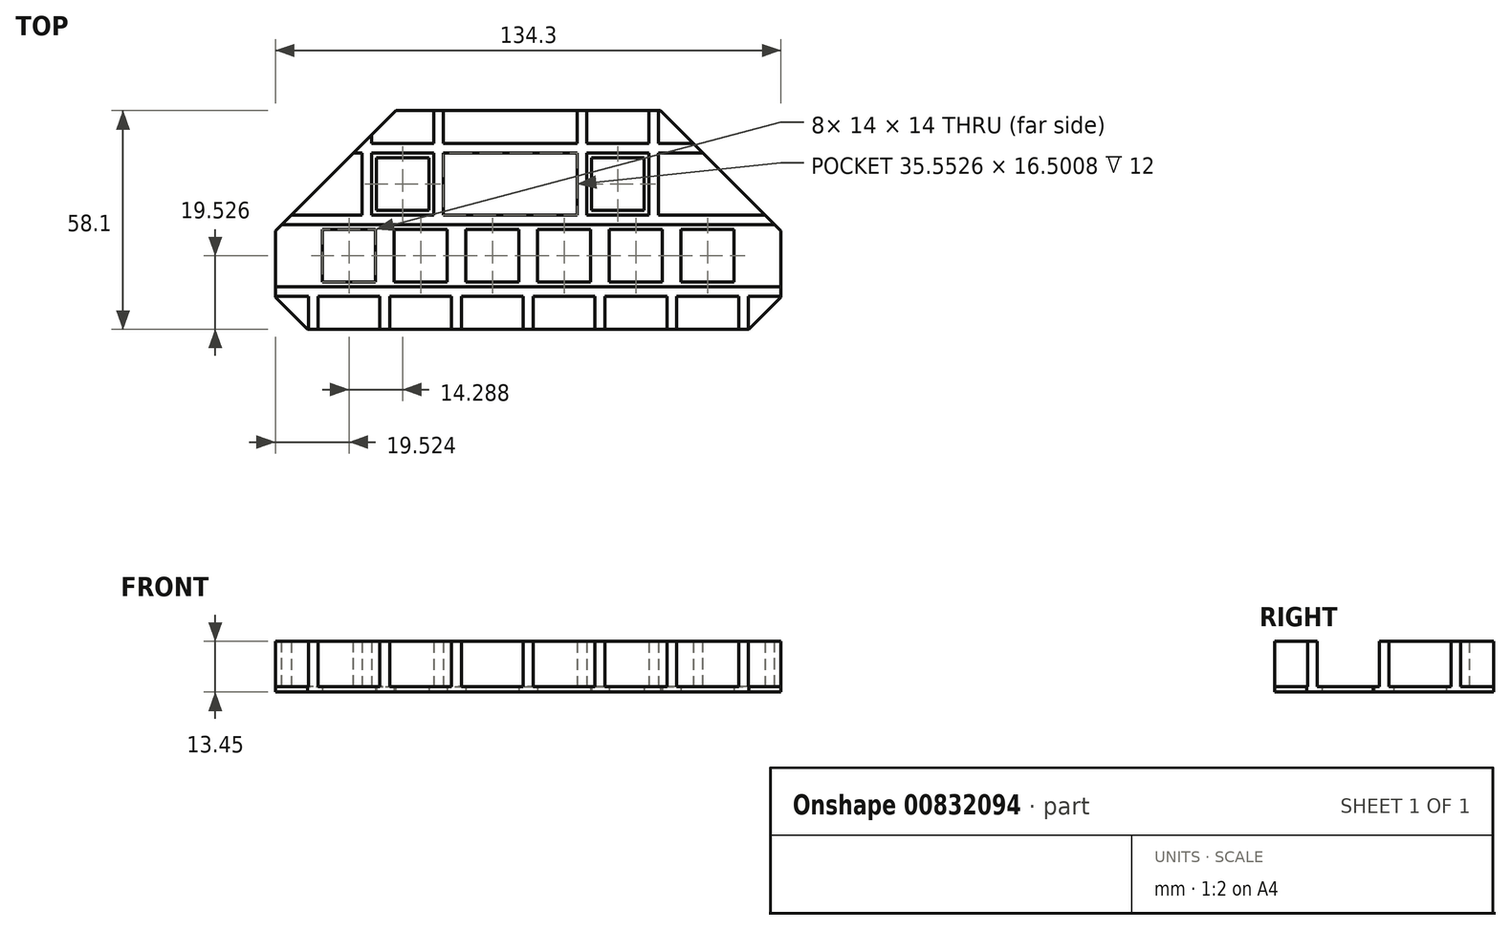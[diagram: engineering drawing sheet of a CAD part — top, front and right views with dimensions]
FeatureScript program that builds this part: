
annotation { "Feature Type Name" : "Feature", "Feature Type Description" : "" }
export const myFeature = defineFeature(function(context is Context, id is Id, definition is map)
    precondition{}
    {
        {
            var Q0;
            Q0=qCreatedBy(makeId("Top.planeOp"),FACE);
            var sketch = newSketch(context, id + "F0", { "sketchPlane" : qUnion([Q0])});
            skLineSegment(sketch, "E0", {"start": v(-57.15, 38.1) * mm, "end": v(57.15, 38.1) * mm});
            skLineSegment(sketch, "E1", {"start": v(57.15, 38.1) * mm, "end": v(57.15, -38.1) * mm});
            skLineSegment(sketch, "E2", {"start": v(57.15, -38.1) * mm, "end": v(-57.15, -38.1) * mm});
            skLineSegment(sketch, "E3", {"start": v(-57.15, -38.1) * mm, "end": v(-57.15, 38.1) * mm});
            skLineSegment(sketch, "E4", {"start": v(-54.63, -21.57) * mm, "end": v(-40.63, -21.57) * mm});
            skLineSegment(sketch, "E5", {"start": v(-40.63, -21.57) * mm, "end": v(-40.63, -35.57) * mm});
            skLineSegment(sketch, "E6", {"start": v(-40.63, -35.57) * mm, "end": v(-54.63, -35.57) * mm});
            skLineSegment(sketch, "E7", {"start": v(-54.63, -35.57) * mm, "end": v(-54.63, -21.57) * mm});
            skLineSegment(sketch, "E8", {"start": v(-35.58, -21.57) * mm, "end": v(-21.58, -21.57) * mm});
            skLineSegment(sketch, "E9", {"start": v(-21.58, -21.57) * mm, "end": v(-21.58, -35.57) * mm});
            skLineSegment(sketch, "E10", {"start": v(-21.58, -35.57) * mm, "end": v(-35.58, -35.57) * mm});
            skLineSegment(sketch, "E11", {"start": v(-35.58, -35.57) * mm, "end": v(-35.58, -21.57) * mm});
            skLineSegment(sketch, "E12", {"start": v(-16.53, -21.57) * mm, "end": v(-2.53, -21.57) * mm});
            skLineSegment(sketch, "E13", {"start": v(-2.53, -21.57) * mm, "end": v(-2.53, -35.57) * mm});
            skLineSegment(sketch, "E14", {"start": v(-2.53, -35.57) * mm, "end": v(-16.53, -35.57) * mm});
            skLineSegment(sketch, "E15", {"start": v(-16.53, -35.57) * mm, "end": v(-16.53, -21.57) * mm});
            skLineSegment(sketch, "E16", {"start": v(2.52, -21.57) * mm, "end": v(16.52, -21.57) * mm});
            skLineSegment(sketch, "E17", {"start": v(16.52, -21.57) * mm, "end": v(16.52, -35.57) * mm});
            skLineSegment(sketch, "E18", {"start": v(16.52, -35.57) * mm, "end": v(2.52, -35.57) * mm});
            skLineSegment(sketch, "E19", {"start": v(2.52, -35.57) * mm, "end": v(2.52, -21.57) * mm});
            skLineSegment(sketch, "E20", {"start": v(21.57, -21.57) * mm, "end": v(35.57, -21.57) * mm});
            skLineSegment(sketch, "E21", {"start": v(35.57, -21.57) * mm, "end": v(35.57, -35.57) * mm});
            skLineSegment(sketch, "E22", {"start": v(35.57, -35.57) * mm, "end": v(21.57, -35.57) * mm});
            skLineSegment(sketch, "E23", {"start": v(21.57, -35.57) * mm, "end": v(21.57, -21.57) * mm});
            skLineSegment(sketch, "E24", {"start": v(40.62, -21.57) * mm, "end": v(54.62, -21.57) * mm});
            skLineSegment(sketch, "E25", {"start": v(54.62, -21.57) * mm, "end": v(54.62, -35.57) * mm});
            skLineSegment(sketch, "E26", {"start": v(54.62, -35.57) * mm, "end": v(40.62, -35.57) * mm});
            skLineSegment(sketch, "E27", {"start": v(40.62, -35.57) * mm, "end": v(40.62, -21.57) * mm});
            skLineSegment(sketch, "E28", {"start": v(-40.34, -2.52) * mm, "end": v(-26.34, -2.52) * mm});
            skLineSegment(sketch, "E29", {"start": v(-26.34, -2.52) * mm, "end": v(-26.34, -16.52) * mm});
            skLineSegment(sketch, "E30", {"start": v(-26.34, -16.52) * mm, "end": v(-40.34, -16.52) * mm});
            skLineSegment(sketch, "E31", {"start": v(-40.34, -16.52) * mm, "end": v(-40.34, -2.52) * mm});
            skLineSegment(sketch, "E32", {"start": v(16.81, -2.52) * mm, "end": v(30.81, -2.52) * mm});
            skLineSegment(sketch, "E33", {"start": v(30.81, -2.52) * mm, "end": v(30.81, -16.52) * mm});
            skLineSegment(sketch, "E34", {"start": v(30.81, -16.52) * mm, "end": v(16.81, -16.52) * mm});
            skLineSegment(sketch, "E35", {"start": v(16.81, -16.52) * mm, "end": v(16.81, -2.52) * mm});
            skLineSegment(sketch, "E36", {"start": v(0, 0) * mm, "end": v(0, 10) * mm});
            skLineSegment(sketch, "E37", {"start": v(0, 10) * mm, "end": v(57.15, 10) * mm});
            skLineSegment(sketch, "E38", {"start": v(0, 10) * mm, "end": v(-57.15, 10) * mm});
            skLineSegment(sketch, "E39", {"start": v(57.15, -38.1) * mm, "end": v(57.15, -48.1) * mm});
            skLineSegment(sketch, "E40", {"start": v(57.15, -48.1) * mm, "end": v(-57.15, -48.1) * mm});
            skLineSegment(sketch, "E41", {"start": v(-57.15, -48.1) * mm, "end": v(-67.15, -48.1) * mm});
            skLineSegment(sketch, "E42", {"start": v(-57.15, 10) * mm, "end": v(-57.15, -38.1) * mm});
            skLineSegment(sketch, "E43", {"start": v(-67.15, -48.1) * mm, "end": v(-67.15, 10) * mm});
            skLineSegment(sketch, "E44", {"start": v(-67.15, 10) * mm, "end": v(-57.15, 10) * mm});
            skLineSegment(sketch, "E45", {"start": v(57.15, -38.1) * mm, "end": v(67.15, -38.1) * mm});
            skLineSegment(sketch, "E46", {"start": v(67.15, -38.1) * mm, "end": v(67.15, 10) * mm});
            skLineSegment(sketch, "E47", {"start": v(67.15, 10) * mm, "end": v(57.15, 10) * mm});
            skLineSegment(sketch, "E48", {"start": v(67.15, -38.1) * mm, "end": v(67.15, -48.1) * mm});
            skLineSegment(sketch, "E49", {"start": v(67.15, -48.1) * mm, "end": v(57.15, -48.1) * mm});
            skSolve(sketch);
        }
        {
            var Q0;
            Q0=makeQuery(id+"F0.imprint","IMPRINT",FACE,{"disambiguationData":[TD([[makeQuery(id+"F0.imprint","IMPRINT",EDGE,{"derivedFrom":sQuery(id+"F0.wireOp",EDGE,"E2")}),1.0]])]});
            var Q1;
            {var subQ0=sQuery(id+"F0.wireOp",EDGE,"E2");Q1=makeQuery(id+"F0.imprint","IMPRINT",FACE,{"disambiguationData":[TD([[makeQuery(id+"F0.imprint","IMPRINT",EDGE,{"derivedFrom":subQ0}),-1.0]])]});}
            var Q2;
            {var subQ0=sQuery(id+"F0.wireOp",EDGE,"E45");Q2=makeQuery(id+"F0.imprint","IMPRINT",FACE,{"disambiguationData":[TD([[makeQuery(id+"F0.imprint","IMPRINT",EDGE,{"derivedFrom":subQ0}),1.0]])]});}
            var Q3;
            Q3=makeQuery(id+"F0.imprint","IMPRINT",FACE,{"disambiguationData":[TD([[makeQuery(id+"F0.imprint","IMPRINT",EDGE,{"derivedFrom":sQuery(id+"F0.wireOp",EDGE,"E39")}),1.0]])]});
            extrude(context, id + "F1", {"entities" : qUnion([Q0, Q1, Q2, Q3]), "depth" : 1.45 * mm, "offsetDistance" : 25 * mm});
        }
        {
            var Q0;
            Q0=makeQuery(id+"F1.opExtrude","CAP_FACE",FACE,{"disambiguationData":[OSD([sQuery(id+"F0.wireOp",EDGE,"E4"),sQuery(id+"F0.wireOp",EDGE,"E5"),sQuery(id+"F0.wireOp",EDGE,"E6"),sQuery(id+"F0.wireOp",EDGE,"E7"),sQuery(id+"F0.wireOp",EDGE,"E8"),sQuery(id+"F0.wireOp",EDGE,"E9"),sQuery(id+"F0.wireOp",EDGE,"E10"),sQuery(id+"F0.wireOp",EDGE,"E11"),sQuery(id+"F0.wireOp",EDGE,"E12"),sQuery(id+"F0.wireOp",EDGE,"E13"),sQuery(id+"F0.wireOp",EDGE,"E14"),sQuery(id+"F0.wireOp",EDGE,"E15"),sQuery(id+"F0.wireOp",EDGE,"E16"),sQuery(id+"F0.wireOp",EDGE,"E17"),sQuery(id+"F0.wireOp",EDGE,"E18"),sQuery(id+"F0.wireOp",EDGE,"E19"),sQuery(id+"F0.wireOp",EDGE,"E20"),sQuery(id+"F0.wireOp",EDGE,"E21"),sQuery(id+"F0.wireOp",EDGE,"E22"),sQuery(id+"F0.wireOp",EDGE,"E23"),sQuery(id+"F0.wireOp",EDGE,"E24"),sQuery(id+"F0.wireOp",EDGE,"E25"),sQuery(id+"F0.wireOp",EDGE,"E26"),sQuery(id+"F0.wireOp",EDGE,"E27"),sQuery(id+"F0.wireOp",EDGE,"E28"),sQuery(id+"F0.wireOp",EDGE,"E29"),sQuery(id+"F0.wireOp",EDGE,"E30"),sQuery(id+"F0.wireOp",EDGE,"E31"),sQuery(id+"F0.wireOp",EDGE,"E32"),sQuery(id+"F0.wireOp",EDGE,"E33"),sQuery(id+"F0.wireOp",EDGE,"E34"),sQuery(id+"F0.wireOp",EDGE,"E35"),sQuery(id+"F0.wireOp",EDGE,"E37"),sQuery(id+"F0.wireOp",EDGE,"E38"),sQuery(id+"F0.wireOp",EDGE,"E40"),sQuery(id+"F0.wireOp",EDGE,"E41"),sQuery(id+"F0.wireOp",EDGE,"E43"),sQuery(id+"F0.wireOp",EDGE,"E44"),sQuery(id+"F0.wireOp",EDGE,"E46"),sQuery(id+"F0.wireOp",EDGE,"E47"),sQuery(id+"F0.wireOp",EDGE,"E48"),sQuery(id+"F0.wireOp",EDGE,"E49")])],"isStart":false});
            var sketch = newSketch(context, id + "F2", { "sketchPlane" : qUnion([Q0])});
            skLineSegment(sketch, "E50", {"start": v(-33.34, -16.52) * mm, "end": v(-33.34, -17.77) * mm});
            skLineSegment(sketch, "E51", {"start": v(-28.58, -21.57) * mm, "end": v(-28.58, -20.32) * mm});
            skLineSegment(sketch, "E52", {"start": v(-28.58, -20.32) * mm, "end": v(67.15, -20.32) * mm});
            skLineSegment(sketch, "E53", {"start": v(-28.58, -20.32) * mm, "end": v(-67.15, -20.32) * mm});
            skLineSegment(sketch, "E54", {"start": v(-33.34, -17.77) * mm, "end": v(67.15, -17.77) * mm});
            skLineSegment(sketch, "E55", {"start": v(-33.34, -17.77) * mm, "end": v(-67.15, -17.77) * mm});
            skLineSegment(sketch, "E56", {"start": v(-40.63, -28.57) * mm, "end": v(-39.38, -28.57) * mm});
            skLineSegment(sketch, "E57", {"start": v(-35.58, -28.57) * mm, "end": v(-36.83, -28.57) * mm});
            skLineSegment(sketch, "E58", {"start": v(-21.58, -28.57) * mm, "end": v(-20.33, -28.57) * mm});
            skLineSegment(sketch, "E59", {"start": v(-16.53, -28.57) * mm, "end": v(-17.78, -28.57) * mm});
            skLineSegment(sketch, "E60", {"start": v(-2.53, -28.57) * mm, "end": v(-1.28, -28.57) * mm});
            skLineSegment(sketch, "E61", {"start": v(2.52, -28.57) * mm, "end": v(1.27, -28.57) * mm});
            skLineSegment(sketch, "E62", {"start": v(16.52, -28.57) * mm, "end": v(17.77, -28.57) * mm});
            skLineSegment(sketch, "E63", {"start": v(21.57, -28.57) * mm, "end": v(20.32, -28.57) * mm});
            skLineSegment(sketch, "E64", {"start": v(40.62, -28.57) * mm, "end": v(39.37, -28.57) * mm});
            skLineSegment(sketch, "E65", {"start": v(35.57, -28.57) * mm, "end": v(36.82, -28.57) * mm});
            skLineSegment(sketch, "E66", {"start": v(-40.34, -9.52) * mm, "end": v(-41.59, -9.52) * mm});
            skLineSegment(sketch, "E67", {"start": v(-26.34, -9.52) * mm, "end": v(-25.09, -9.52) * mm});
            skLineSegment(sketch, "E68", {"start": v(16.81, -9.52) * mm, "end": v(15.56, -9.52) * mm});
            skLineSegment(sketch, "E69", {"start": v(30.81, -9.52) * mm, "end": v(32.06, -9.52) * mm});
            skLineSegment(sketch, "E70", {"start": v(32.06, -9.52) * mm, "end": v(32.06, 10) * mm});
            skLineSegment(sketch, "E71", {"start": v(32.06, -9.52) * mm, "end": v(32.06, -17.77) * mm});
            skLineSegment(sketch, "E72", {"start": v(67.15, -17.77) * mm, "end": v(67.15, -20.32) * mm});
            skLineSegment(sketch, "E73", {"start": v(32.06, -9.52) * mm, "end": v(34.61, -9.52) * mm});
            skLineSegment(sketch, "E74", {"start": v(34.61, -9.52) * mm, "end": v(34.61, -17.77) * mm});
            skLineSegment(sketch, "E75", {"start": v(34.61, -9.52) * mm, "end": v(34.61, 10) * mm});
            skLineSegment(sketch, "E76", {"start": v(15.56, -9.52) * mm, "end": v(15.56, -17.77) * mm});
            skLineSegment(sketch, "E77", {"start": v(15.56, -17.77) * mm, "end": v(13.01, -17.77) * mm});
            skLineSegment(sketch, "E78", {"start": v(13.01, -17.77) * mm, "end": v(13.01, 10) * mm});
            skLineSegment(sketch, "E79", {"start": v(15.56, -9.52) * mm, "end": v(15.56, 10) * mm});
            skLineSegment(sketch, "E80", {"start": v(15.56, 10) * mm, "end": v(13.01, 10) * mm});
            skLineSegment(sketch, "E81", {"start": v(32.06, 10) * mm, "end": v(34.61, 10) * mm});
            skLineSegment(sketch, "E82", {"start": v(-25.09, -9.52) * mm, "end": v(-25.09, -17.77) * mm});
            skLineSegment(sketch, "E83", {"start": v(-25.09, -9.52) * mm, "end": v(-25.09, 10) * mm});
            skLineSegment(sketch, "E84", {"start": v(-25.09, 10) * mm, "end": v(-22.54, 10) * mm});
            skLineSegment(sketch, "E85", {"start": v(-22.54, 10) * mm, "end": v(-22.54, -17.77) * mm});
            skLineSegment(sketch, "E86", {"start": v(-41.59, -9.52) * mm, "end": v(-41.59, 10) * mm});
            skLineSegment(sketch, "E87", {"start": v(-41.59, 10) * mm, "end": v(-44.14, 10) * mm});
            skLineSegment(sketch, "E88", {"start": v(-44.14, 10) * mm, "end": v(-44.14, -17.77) * mm});
            skLineSegment(sketch, "E89", {"start": v(-41.59, -9.52) * mm, "end": v(-41.59, -17.77) * mm});
            skLineSegment(sketch, "E90", {"start": v(-39.38, -28.57) * mm, "end": v(-39.38, -48.1) * mm});
            skLineSegment(sketch, "E91", {"start": v(-39.38, -48.1) * mm, "end": v(-36.83, -48.1) * mm});
            skLineSegment(sketch, "E92", {"start": v(-36.83, -48.1) * mm, "end": v(-36.83, -20.32) * mm});
            skLineSegment(sketch, "E93", {"start": v(-36.83, -20.32) * mm, "end": v(-39.38, -20.32) * mm});
            skLineSegment(sketch, "E94", {"start": v(-39.38, -20.32) * mm, "end": v(-39.38, -28.57) * mm});
            skLineSegment(sketch, "E95", {"start": v(-20.33, -28.57) * mm, "end": v(-20.33, -48.1) * mm});
            skLineSegment(sketch, "E96", {"start": v(-20.33, -48.1) * mm, "end": v(-17.78, -48.1) * mm});
            skLineSegment(sketch, "E97", {"start": v(-17.78, -48.1) * mm, "end": v(-17.78, -20.32) * mm});
            skLineSegment(sketch, "E98", {"start": v(-17.78, -20.32) * mm, "end": v(-20.33, -20.32) * mm});
            skLineSegment(sketch, "E99", {"start": v(-20.33, -20.32) * mm, "end": v(-20.33, -28.57) * mm});
            skLineSegment(sketch, "E100", {"start": v(-1.28, -28.57) * mm, "end": v(-1.28, -48.1) * mm});
            skLineSegment(sketch, "E101", {"start": v(-1.28, -48.1) * mm, "end": v(1.27, -48.1) * mm});
            skLineSegment(sketch, "E102", {"start": v(1.27, -48.1) * mm, "end": v(1.27, -20.32) * mm});
            skLineSegment(sketch, "E103", {"start": v(1.27, -20.32) * mm, "end": v(-1.28, -20.32) * mm});
            skLineSegment(sketch, "E104", {"start": v(-1.28, -20.32) * mm, "end": v(-1.28, -28.57) * mm});
            skLineSegment(sketch, "E105", {"start": v(17.77, -28.57) * mm, "end": v(17.77, -48.1) * mm});
            skLineSegment(sketch, "E106", {"start": v(17.77, -48.1) * mm, "end": v(20.32, -48.1) * mm});
            skLineSegment(sketch, "E107", {"start": v(20.32, -48.1) * mm, "end": v(20.32, -20.32) * mm});
            skLineSegment(sketch, "E108", {"start": v(20.32, -20.32) * mm, "end": v(17.77, -20.32) * mm});
            skLineSegment(sketch, "E109", {"start": v(17.77, -20.32) * mm, "end": v(17.77, -28.57) * mm});
            skLineSegment(sketch, "E110", {"start": v(36.82, -28.57) * mm, "end": v(36.82, -48.1) * mm});
            skLineSegment(sketch, "E111", {"start": v(36.82, -48.1) * mm, "end": v(39.37, -48.1) * mm});
            skLineSegment(sketch, "E112", {"start": v(39.37, -48.1) * mm, "end": v(39.37, -20.32) * mm});
            skLineSegment(sketch, "E113", {"start": v(39.37, -20.32) * mm, "end": v(36.82, -20.32) * mm});
            skLineSegment(sketch, "E114", {"start": v(36.82, -20.32) * mm, "end": v(36.82, -28.57) * mm});
            skLineSegment(sketch, "E115", {"start": v(54.62, -28.57) * mm, "end": v(55.87, -28.57) * mm});
            skLineSegment(sketch, "E116", {"start": v(55.87, -28.57) * mm, "end": v(55.87, -48.1) * mm});
            skLineSegment(sketch, "E117", {"start": v(55.87, -48.1) * mm, "end": v(58.42, -48.1) * mm});
            skLineSegment(sketch, "E118", {"start": v(58.42, -48.1) * mm, "end": v(58.42, -20.32) * mm});
            skLineSegment(sketch, "E119", {"start": v(58.42, -20.32) * mm, "end": v(55.87, -20.32) * mm});
            skLineSegment(sketch, "E120", {"start": v(55.87, -20.32) * mm, "end": v(55.87, -28.57) * mm});
            skLineSegment(sketch, "E121", {"start": v(-54.63, -28.57) * mm, "end": v(-55.88, -28.57) * mm});
            skLineSegment(sketch, "E122", {"start": v(-55.88, -28.57) * mm, "end": v(-55.88, -48.1) * mm});
            skLineSegment(sketch, "E123", {"start": v(-55.88, -48.1) * mm, "end": v(-58.42, -48.1) * mm});
            skLineSegment(sketch, "E124", {"start": v(-58.42, -48.1) * mm, "end": v(-58.42, -20.32) * mm});
            skLineSegment(sketch, "E125", {"start": v(-58.42, -20.32) * mm, "end": v(-55.88, -20.32) * mm});
            skLineSegment(sketch, "E126", {"start": v(-55.88, -20.32) * mm, "end": v(-55.88, -28.57) * mm});
            skLineSegment(sketch, "E127", {"start": v(-47.63, -35.57) * mm, "end": v(-47.63, -36.82) * mm});
            skLineSegment(sketch, "E128", {"start": v(-47.63, -36.82) * mm, "end": v(67.15, -36.82) * mm});
            skLineSegment(sketch, "E129", {"start": v(67.15, -36.82) * mm, "end": v(67.15, -39.37) * mm});
            skLineSegment(sketch, "E130", {"start": v(67.15, -39.37) * mm, "end": v(-67.15, -39.37) * mm});
            skLineSegment(sketch, "E131", {"start": v(-47.63, -36.82) * mm, "end": v(-67.15, -36.82) * mm});
            skLineSegment(sketch, "E132", {"start": v(-67.15, -36.82) * mm, "end": v(-67.15, -39.37) * mm});
            skLineSegment(sketch, "E133", {"start": v(-33.34, -2.52) * mm, "end": v(-33.34, -1.27) * mm});
            skLineSegment(sketch, "E134", {"start": v(-33.34, -1.27) * mm, "end": v(67.15, -1.27) * mm});
            skLineSegment(sketch, "E135", {"start": v(67.15, -1.27) * mm, "end": v(67.15, 1.28) * mm});
            skLineSegment(sketch, "E136", {"start": v(67.15, 1.28) * mm, "end": v(-67.15, 1.28) * mm});
            skLineSegment(sketch, "E137", {"start": v(-67.15, -17.77) * mm, "end": v(-67.15, -20.32) * mm});
            skLineSegment(sketch, "E138", {"start": v(-33.34, -1.27) * mm, "end": v(-67.15, -1.27) * mm});
            skLineSegment(sketch, "E139", {"start": v(-67.15, -1.27) * mm, "end": v(-67.15, 1.28) * mm});
            skSolve(sketch);
        }
        {
            var Q0;
            {var subQ5=sQuery(id+"F2.wireOp",EDGE,"E132");Q0=makeQuery(id+"F2.imprint","IMPRINT",FACE,{"disambiguationData":[TD([[makeQuery(id+"F2.imprint","IMPRINT",EDGE,{"derivedFrom":subQ5}),-1.0]])]});}
            var Q1;
            {var subQ0=sQuery(id+"F2.wireOp",EDGE,"E123");Q1=makeQuery(id+"F2.imprint","IMPRINT",FACE,{"disambiguationData":[TD([[makeQuery(id+"F2.imprint","IMPRINT",EDGE,{"derivedFrom":subQ0}),-1.0]])]});}
            var Q2;
            {var subQ0=sQuery(id+"F2.wireOp",EDGE,"E131");var subQ1=sQuery(id+"F2.wireOp",EDGE,"E122");var subQ2=makeQuery(id+"F2.imprint","INTERSECT",VERTEX,{"derivedFrom":[subQ1,subQ0]});Q2=makeQuery(id+"F2.imprint","IMPRINT",FACE,{"disambiguationData":[TD([[makeQuery(id+"F2.imprint","IMPRINT",EDGE,{"disambiguationData":[TD([[subQ2,-1.0]])],"derivedFrom":subQ1}),-1.0]])]});}
            var Q3;
            {var subQ1=sQuery(id+"F2.wireOp",EDGE,"E125");Q3=makeQuery(id+"F2.imprint","IMPRINT",FACE,{"disambiguationData":[TD([[makeQuery(id+"F2.imprint","IMPRINT",EDGE,{"derivedFrom":subQ1}),-1.0]])]});}
            var Q4;
            {var subQ8=sQuery(id+"F2.wireOp",EDGE,"E72");Q4=makeQuery(id+"F2.imprint","IMPRINT",FACE,{"disambiguationData":[TD([[makeQuery(id+"F2.imprint","IMPRINT",EDGE,{"derivedFrom":subQ8}),1.0]])]});}
            var Q5;
            {var subQ1=sQuery(id+"F2.wireOp",EDGE,"E128");var subQ3=sQuery(id+"F2.wireOp",EDGE,"E90");var subQ4=makeQuery(id+"F2.imprint","INTERSECT",VERTEX,{"derivedFrom":[subQ3,subQ1]});Q5=makeQuery(id+"F2.imprint","IMPRINT",FACE,{"disambiguationData":[TD([[makeQuery(id+"F2.imprint","IMPRINT",EDGE,{"disambiguationData":[TD([[subQ4,-1.0]])],"derivedFrom":subQ3}),-1.0]])]});}
            var Q6;
            {var subQ0=sQuery(id+"F2.wireOp",EDGE,"E128");var subQ1=sQuery(id+"F2.wireOp",EDGE,"E90");var subQ2=makeQuery(id+"F2.imprint","INTERSECT",VERTEX,{"derivedFrom":[subQ1,subQ0]});Q6=makeQuery(id+"F2.imprint","IMPRINT",FACE,{"disambiguationData":[TD([[makeQuery(id+"F2.imprint","IMPRINT",EDGE,{"disambiguationData":[TD([[subQ2,-1.0]])],"derivedFrom":subQ1}),1.0]])]});}
            var Q7;
            {var subQ0=sQuery(id+"F2.wireOp",EDGE,"E130");var subQ1=sQuery(id+"F2.wireOp",EDGE,"E92");var subQ2=makeQuery(id+"F2.imprint","INTERSECT",VERTEX,{"derivedFrom":[subQ1,subQ0]});Q7=makeQuery(id+"F2.imprint","IMPRINT",FACE,{"disambiguationData":[TD([[makeQuery(id+"F2.imprint","IMPRINT",EDGE,{"disambiguationData":[TD([[subQ2,-1.0]])],"derivedFrom":subQ1}),-1.0]])]});}
            var Q8;
            {var subQ0=sQuery(id+"F2.wireOp",EDGE,"E91");Q8=makeQuery(id+"F2.imprint","IMPRINT",FACE,{"disambiguationData":[TD([[makeQuery(id+"F2.imprint","IMPRINT",EDGE,{"derivedFrom":subQ0}),-1.0]])]});}
            var Q9;
            {var subQ1=sQuery(id+"F2.wireOp",EDGE,"E93");Q9=makeQuery(id+"F2.imprint","IMPRINT",FACE,{"disambiguationData":[TD([[makeQuery(id+"F2.imprint","IMPRINT",EDGE,{"derivedFrom":subQ1}),1.0]])]});}
            var Q10;
            {var subQ0=sQuery(id+"F2.wireOp",EDGE,"E89");Q10=makeQuery(id+"F2.imprint","IMPRINT",FACE,{"disambiguationData":[TD([[makeQuery(id+"F2.imprint","IMPRINT",EDGE,{"derivedFrom":subQ0}),-1.0]])]});}
            var Q11;
            {var subQ5=sQuery(id+"F2.wireOp",EDGE,"E82");Q11=makeQuery(id+"F2.imprint","IMPRINT",FACE,{"disambiguationData":[TD([[makeQuery(id+"F2.imprint","IMPRINT",EDGE,{"derivedFrom":subQ5}),1.0]])]});}
            var Q12;
            {var subQ1=sQuery(id+"F2.wireOp",EDGE,"E134");var subQ3=sQuery(id+"F2.wireOp",EDGE,"E83");var subQ4=makeQuery(id+"F2.imprint","INTERSECT",VERTEX,{"derivedFrom":[subQ3,subQ1]});Q12=makeQuery(id+"F2.imprint","IMPRINT",FACE,{"disambiguationData":[TD([[makeQuery(id+"F2.imprint","IMPRINT",EDGE,{"disambiguationData":[TD([[subQ4,-1.0]])],"derivedFrom":subQ3}),1.0]])]});}
            var Q13;
            {var subQ0=sQuery(id+"F2.wireOp",EDGE,"E138");var subQ1=sQuery(id+"F2.wireOp",EDGE,"E86");var subQ2=makeQuery(id+"F2.imprint","INTERSECT",VERTEX,{"derivedFrom":[subQ1,subQ0]});Q13=makeQuery(id+"F2.imprint","IMPRINT",FACE,{"disambiguationData":[TD([[makeQuery(id+"F2.imprint","IMPRINT",EDGE,{"disambiguationData":[TD([[subQ2,-1.0]])],"derivedFrom":subQ1}),1.0]])]});}
            var Q14;
            {var subQ0=sQuery(id+"F2.wireOp",EDGE,"E134");var subQ1=sQuery(id+"F2.wireOp",EDGE,"E83");var subQ2=makeQuery(id+"F2.imprint","INTERSECT",VERTEX,{"derivedFrom":[subQ1,subQ0]});Q14=makeQuery(id+"F2.imprint","IMPRINT",FACE,{"disambiguationData":[TD([[makeQuery(id+"F2.imprint","IMPRINT",EDGE,{"disambiguationData":[TD([[subQ2,-1.0]])],"derivedFrom":subQ1}),-1.0]])]});}
            var Q15;
            {var subQ0=sQuery(id+"F2.wireOp",EDGE,"E134");var subQ1=sQuery(id+"F2.wireOp",EDGE,"E78");var subQ2=makeQuery(id+"F2.imprint","INTERSECT",VERTEX,{"derivedFrom":[subQ1,subQ0]});Q15=makeQuery(id+"F2.imprint","IMPRINT",FACE,{"disambiguationData":[TD([[makeQuery(id+"F2.imprint","IMPRINT",EDGE,{"disambiguationData":[TD([[subQ2,-1.0]])],"derivedFrom":subQ1}),1.0]])]});}
            var Q16;
            {var subQ5=sQuery(id+"F2.wireOp",EDGE,"E139");Q16=makeQuery(id+"F2.imprint","IMPRINT",FACE,{"disambiguationData":[TD([[makeQuery(id+"F2.imprint","IMPRINT",EDGE,{"derivedFrom":subQ5}),-1.0]])]});}
            var Q17;
            {var subQ0=sQuery(id+"F2.wireOp",EDGE,"E134");var subQ1=sQuery(id+"F2.wireOp",EDGE,"E70");var subQ2=makeQuery(id+"F2.imprint","INTERSECT",VERTEX,{"derivedFrom":[subQ1,subQ0]});Q17=makeQuery(id+"F2.imprint","IMPRINT",FACE,{"disambiguationData":[TD([[makeQuery(id+"F2.imprint","IMPRINT",EDGE,{"disambiguationData":[TD([[subQ2,-1.0]])],"derivedFrom":subQ1}),1.0]])]});}
            var Q18;
            {var subQ0=sQuery(id+"F2.wireOp",EDGE,"E134");var subQ1=sQuery(id+"F2.wireOp",EDGE,"E78");var subQ2=makeQuery(id+"F2.imprint","INTERSECT",VERTEX,{"derivedFrom":[subQ1,subQ0]});Q18=makeQuery(id+"F2.imprint","IMPRINT",FACE,{"disambiguationData":[TD([[makeQuery(id+"F2.imprint","IMPRINT",EDGE,{"disambiguationData":[TD([[subQ2,-1.0]])],"derivedFrom":subQ1}),-1.0]])]});}
            var Q19;
            {var subQ0=sQuery(id+"F2.wireOp",EDGE,"E134");var subQ1=sQuery(id+"F2.wireOp",EDGE,"E70");var subQ2=makeQuery(id+"F2.imprint","INTERSECT",VERTEX,{"derivedFrom":[subQ1,subQ0]});Q19=makeQuery(id+"F2.imprint","IMPRINT",FACE,{"disambiguationData":[TD([[makeQuery(id+"F2.imprint","IMPRINT",EDGE,{"disambiguationData":[TD([[subQ2,-1.0]])],"derivedFrom":subQ1}),-1.0]])]});}
            var Q20;
            {var subQ5=sQuery(id+"F2.wireOp",EDGE,"E135");Q20=makeQuery(id+"F2.imprint","IMPRINT",FACE,{"disambiguationData":[TD([[makeQuery(id+"F2.imprint","IMPRINT",EDGE,{"derivedFrom":subQ5}),1.0]])]});}
            var Q21;
            {var subQ1=sQuery(id+"F2.wireOp",EDGE,"E119");Q21=makeQuery(id+"F2.imprint","IMPRINT",FACE,{"disambiguationData":[TD([[makeQuery(id+"F2.imprint","IMPRINT",EDGE,{"derivedFrom":subQ1}),1.0]])]});}
            var Q22;
            {var subQ5=sQuery(id+"F2.wireOp",EDGE,"E129");Q22=makeQuery(id+"F2.imprint","IMPRINT",FACE,{"disambiguationData":[TD([[makeQuery(id+"F2.imprint","IMPRINT",EDGE,{"derivedFrom":subQ5}),1.0]])]});}
            var Q23;
            {var subQ0=sQuery(id+"F2.wireOp",EDGE,"E128");var subQ1=sQuery(id+"F2.wireOp",EDGE,"E116");var subQ2=makeQuery(id+"F2.imprint","INTERSECT",VERTEX,{"derivedFrom":[subQ1,subQ0]});Q23=makeQuery(id+"F2.imprint","IMPRINT",FACE,{"disambiguationData":[TD([[makeQuery(id+"F2.imprint","IMPRINT",EDGE,{"disambiguationData":[TD([[subQ2,-1.0]])],"derivedFrom":subQ1}),1.0]])]});}
            var Q24;
            {var subQ0=sQuery(id+"F2.wireOp",EDGE,"E117");Q24=makeQuery(id+"F2.imprint","IMPRINT",FACE,{"disambiguationData":[TD([[makeQuery(id+"F2.imprint","IMPRINT",EDGE,{"derivedFrom":subQ0}),-1.0]])]});}
            var Q25;
            {var subQ0=sQuery(id+"F2.wireOp",EDGE,"E130");var subQ1=sQuery(id+"F2.wireOp",EDGE,"E112");var subQ2=makeQuery(id+"F2.imprint","INTERSECT",VERTEX,{"derivedFrom":[subQ1,subQ0]});Q25=makeQuery(id+"F2.imprint","IMPRINT",FACE,{"disambiguationData":[TD([[makeQuery(id+"F2.imprint","IMPRINT",EDGE,{"disambiguationData":[TD([[subQ2,-1.0]])],"derivedFrom":subQ1}),-1.0]])]});}
            var Q26;
            {var subQ1=sQuery(id+"F2.wireOp",EDGE,"E113");Q26=makeQuery(id+"F2.imprint","IMPRINT",FACE,{"disambiguationData":[TD([[makeQuery(id+"F2.imprint","IMPRINT",EDGE,{"derivedFrom":subQ1}),1.0]])]});}
            var Q27;
            {var subQ0=sQuery(id+"F2.wireOp",EDGE,"E128");var subQ1=sQuery(id+"F2.wireOp",EDGE,"E110");var subQ2=makeQuery(id+"F2.imprint","INTERSECT",VERTEX,{"derivedFrom":[subQ1,subQ0]});Q27=makeQuery(id+"F2.imprint","IMPRINT",FACE,{"disambiguationData":[TD([[makeQuery(id+"F2.imprint","IMPRINT",EDGE,{"disambiguationData":[TD([[subQ2,-1.0]])],"derivedFrom":subQ1}),1.0]])]});}
            var Q28;
            {var subQ0=sQuery(id+"F2.wireOp",EDGE,"E111");Q28=makeQuery(id+"F2.imprint","IMPRINT",FACE,{"disambiguationData":[TD([[makeQuery(id+"F2.imprint","IMPRINT",EDGE,{"derivedFrom":subQ0}),-1.0]])]});}
            var Q29;
            {var subQ0=sQuery(id+"F2.wireOp",EDGE,"E130");var subQ1=sQuery(id+"F2.wireOp",EDGE,"E107");var subQ2=makeQuery(id+"F2.imprint","INTERSECT",VERTEX,{"derivedFrom":[subQ1,subQ0]});Q29=makeQuery(id+"F2.imprint","IMPRINT",FACE,{"disambiguationData":[TD([[makeQuery(id+"F2.imprint","IMPRINT",EDGE,{"disambiguationData":[TD([[subQ2,-1.0]])],"derivedFrom":subQ1}),-1.0]])]});}
            var Q30;
            {var subQ1=sQuery(id+"F2.wireOp",EDGE,"E108");Q30=makeQuery(id+"F2.imprint","IMPRINT",FACE,{"disambiguationData":[TD([[makeQuery(id+"F2.imprint","IMPRINT",EDGE,{"derivedFrom":subQ1}),1.0]])]});}
            var Q31;
            {var subQ0=sQuery(id+"F2.wireOp",EDGE,"E106");Q31=makeQuery(id+"F2.imprint","IMPRINT",FACE,{"disambiguationData":[TD([[makeQuery(id+"F2.imprint","IMPRINT",EDGE,{"derivedFrom":subQ0}),-1.0]])]});}
            var Q32;
            {var subQ0=sQuery(id+"F2.wireOp",EDGE,"E128");var subQ1=sQuery(id+"F2.wireOp",EDGE,"E105");var subQ2=makeQuery(id+"F2.imprint","INTERSECT",VERTEX,{"derivedFrom":[subQ1,subQ0]});Q32=makeQuery(id+"F2.imprint","IMPRINT",FACE,{"disambiguationData":[TD([[makeQuery(id+"F2.imprint","IMPRINT",EDGE,{"disambiguationData":[TD([[subQ2,-1.0]])],"derivedFrom":subQ1}),1.0]])]});}
            var Q33;
            {var subQ6=sQuery(id+"F2.wireOp",EDGE,"E103");Q33=makeQuery(id+"F2.imprint","IMPRINT",FACE,{"disambiguationData":[TD([[makeQuery(id+"F2.imprint","IMPRINT",EDGE,{"derivedFrom":subQ6}),1.0]])]});}
            var Q34;
            {var subQ0=sQuery(id+"F2.wireOp",EDGE,"E130");var subQ1=sQuery(id+"F2.wireOp",EDGE,"E102");var subQ2=makeQuery(id+"F2.imprint","INTERSECT",VERTEX,{"derivedFrom":[subQ1,subQ0]});Q34=makeQuery(id+"F2.imprint","IMPRINT",FACE,{"disambiguationData":[TD([[makeQuery(id+"F2.imprint","IMPRINT",EDGE,{"disambiguationData":[TD([[subQ2,-1.0]])],"derivedFrom":subQ1}),-1.0]])]});}
            var Q35;
            {var subQ0=sQuery(id+"F2.wireOp",EDGE,"E128");var subQ1=sQuery(id+"F2.wireOp",EDGE,"E100");var subQ2=makeQuery(id+"F2.imprint","INTERSECT",VERTEX,{"derivedFrom":[subQ1,subQ0]});Q35=makeQuery(id+"F2.imprint","IMPRINT",FACE,{"disambiguationData":[TD([[makeQuery(id+"F2.imprint","IMPRINT",EDGE,{"disambiguationData":[TD([[subQ2,-1.0]])],"derivedFrom":subQ1}),1.0]])]});}
            var Q36;
            {var subQ0=sQuery(id+"F2.wireOp",EDGE,"E130");var subQ1=sQuery(id+"F2.wireOp",EDGE,"E97");var subQ2=makeQuery(id+"F2.imprint","INTERSECT",VERTEX,{"derivedFrom":[subQ1,subQ0]});Q36=makeQuery(id+"F2.imprint","IMPRINT",FACE,{"disambiguationData":[TD([[makeQuery(id+"F2.imprint","IMPRINT",EDGE,{"disambiguationData":[TD([[subQ2,-1.0]])],"derivedFrom":subQ1}),-1.0]])]});}
            var Q37;
            {var subQ0=sQuery(id+"F2.wireOp",EDGE,"E128");var subQ1=sQuery(id+"F2.wireOp",EDGE,"E95");var subQ2=makeQuery(id+"F2.imprint","INTERSECT",VERTEX,{"derivedFrom":[subQ1,subQ0]});Q37=makeQuery(id+"F2.imprint","IMPRINT",FACE,{"disambiguationData":[TD([[makeQuery(id+"F2.imprint","IMPRINT",EDGE,{"disambiguationData":[TD([[subQ2,-1.0]])],"derivedFrom":subQ1}),1.0]])]});}
            var Q38;
            {var subQ1=sQuery(id+"F2.wireOp",EDGE,"E98");Q38=makeQuery(id+"F2.imprint","IMPRINT",FACE,{"disambiguationData":[TD([[makeQuery(id+"F2.imprint","IMPRINT",EDGE,{"derivedFrom":subQ1}),1.0]])]});}
            var Q39;
            {var subQ0=sQuery(id+"F2.wireOp",EDGE,"E71");Q39=makeQuery(id+"F2.imprint","IMPRINT",FACE,{"disambiguationData":[TD([[makeQuery(id+"F2.imprint","IMPRINT",EDGE,{"derivedFrom":subQ0}),1.0]])]});}
            var Q40;
            {var subQ5=sQuery(id+"F2.wireOp",EDGE,"E76");Q40=makeQuery(id+"F2.imprint","IMPRINT",FACE,{"disambiguationData":[TD([[makeQuery(id+"F2.imprint","IMPRINT",EDGE,{"derivedFrom":subQ5}),-1.0]])]});}
            var Q41;
            {var subQ0=sQuery(id+"F2.wireOp",EDGE,"E73");Q41=makeQuery(id+"F2.imprint","IMPRINT",FACE,{"disambiguationData":[TD([[makeQuery(id+"F2.imprint","IMPRINT",EDGE,{"derivedFrom":subQ0}),1.0]])]});}
            var Q42;
            {var subQ0=sQuery(id+"F2.wireOp",EDGE,"E81");Q42=makeQuery(id+"F2.imprint","IMPRINT",FACE,{"disambiguationData":[TD([[makeQuery(id+"F2.imprint","IMPRINT",EDGE,{"derivedFrom":subQ0}),-1.0]])]});}
            var Q43;
            {var subQ0=sQuery(id+"F2.wireOp",EDGE,"E80");Q43=makeQuery(id+"F2.imprint","IMPRINT",FACE,{"disambiguationData":[TD([[makeQuery(id+"F2.imprint","IMPRINT",EDGE,{"derivedFrom":subQ0}),-1.0]])]});}
            var Q44;
            {var subQ0=sQuery(id+"F2.wireOp",EDGE,"E84");Q44=makeQuery(id+"F2.imprint","IMPRINT",FACE,{"disambiguationData":[TD([[makeQuery(id+"F2.imprint","IMPRINT",EDGE,{"derivedFrom":subQ0}),-1.0]])]});}
            var Q45;
            {var subQ0=sQuery(id+"F2.wireOp",EDGE,"E87");Q45=makeQuery(id+"F2.imprint","IMPRINT",FACE,{"disambiguationData":[TD([[makeQuery(id+"F2.imprint","IMPRINT",EDGE,{"derivedFrom":subQ0}),-1.0]])]});}
            var Q46;
            {var subQ0=sQuery(id+"F2.wireOp",EDGE,"E96");Q46=makeQuery(id+"F2.imprint","IMPRINT",FACE,{"disambiguationData":[TD([[makeQuery(id+"F2.imprint","IMPRINT",EDGE,{"derivedFrom":subQ0}),-1.0]])]});}
            var Q47;
            {var subQ0=sQuery(id+"F2.wireOp",EDGE,"E101");Q47=makeQuery(id+"F2.imprint","IMPRINT",FACE,{"disambiguationData":[TD([[makeQuery(id+"F2.imprint","IMPRINT",EDGE,{"derivedFrom":subQ0}),-1.0]])]});}
            extrude(context, id + "F3", {"entities" : qUnion([Q0, Q1, Q2, Q3, Q4, Q5, Q6, Q7, Q8, Q9, Q10, Q11, Q12, Q13, Q14, Q15, Q16, Q17, Q18, Q19, Q20, Q21, Q22, Q23, Q24, Q25, Q26, Q27, Q28, Q29, Q30, Q31, Q32, Q33, Q34, Q35, Q36, Q37, Q38, Q39, Q40, Q41, Q42, Q43, Q44, Q45, Q46, Q47]), "operationType" : NewBodyOperationType.ADD, "depth" : 12 * mm, "offsetDistance" : 25 * mm});
        }
        {
            var Q0;
            Q0=makeQuery(id+"F1.opExtrude","SWEPT_EDGE",EDGE,{"disambiguationData":[OSD([sQuery(id+"F0.wireOp",EDGE,"E43"),sQuery(id+"F0.wireOp",EDGE,"E44")])]});
            var Q1;
            Q1=makeQuery(id+"F1.opExtrude","SWEPT_EDGE",EDGE,{"disambiguationData":[OSD([sQuery(id+"F0.wireOp",EDGE,"E46"),sQuery(id+"F0.wireOp",EDGE,"E47")])]});
            chamfer(context, id + "F4", {"entities" : qUnion([Q0, Q1]), "width" : 32 * mm, "tangentPropagation" : true});
        }
        {
            var Q0;
            Q0=makeQuery(id+"F1.opExtrude","SWEPT_EDGE",EDGE,{"disambiguationData":[OSD([sQuery(id+"F0.wireOp",EDGE,"E41"),sQuery(id+"F0.wireOp",EDGE,"E43")])]});
            var Q1;
            Q1=makeQuery(id+"F1.opExtrude","SWEPT_EDGE",EDGE,{"disambiguationData":[OSD([sQuery(id+"F0.wireOp",EDGE,"E48"),sQuery(id+"F0.wireOp",EDGE,"E49")])]});
            chamfer(context, id + "F5", {"entities" : qUnion([Q0, Q1]), "width" : 8.5 * mm, "tangentPropagation" : true});
        }
    });
